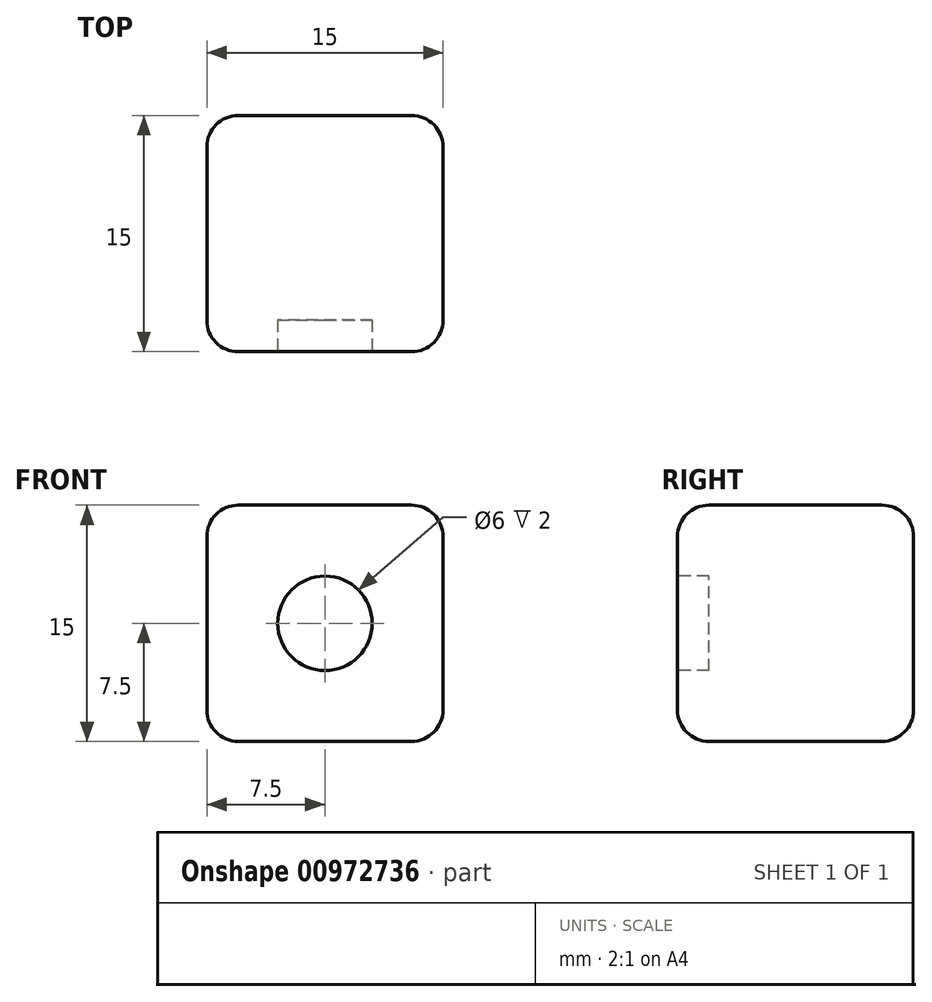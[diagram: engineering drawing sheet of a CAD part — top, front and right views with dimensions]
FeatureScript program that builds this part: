
annotation { "Feature Type Name" : "Feature", "Feature Type Description" : "" }
export const myFeature = defineFeature(function(context is Context, id is Id, definition is map)
    precondition{}
    {
        {
            var Q0;
            Q0=qCreatedBy(makeId("Front.planeOp"),FACE);
            var sketch = newSketch(context, id + "F0", { "sketchPlane" : qUnion([Q0])});
            skLineSegment(sketch, "E0.bottom", {"start": v(-7.5, 7.5) * mm, "end": v(7.5, 7.5) * mm});
            skLineSegment(sketch, "E0.top", {"start": v(-7.5, -7.5) * mm, "end": v(7.5, -7.5) * mm});
            skLineSegment(sketch, "E0.left", {"start": v(-7.5, 7.5) * mm, "end": v(-7.5, -7.5) * mm});
            skLineSegment(sketch, "E0.right", {"start": v(7.5, 7.5) * mm, "end": v(7.5, -7.5) * mm});
            skLineSegment(sketch, "E1", {"start": v(-7.5, 0) * mm, "end": v(7.5, 0) * mm, "construction": true});
            skLineSegment(sketch, "E2", {"start": v(0, 7.5) * mm, "end": v(0, -7.5) * mm, "construction": true});
            skPoint(sketch, "E3", {"position": v(0, 0) * mm});
            skSolve(sketch);
        }
        {
            var Q0;
            Q0=makeQuery(id+"F0.imprint","IMPRINT",FACE,{"disambiguationData":[TD([[makeQuery(id+"F0.imprint","IMPRINT",EDGE,{"derivedFrom":sQuery(id+"F0.wireOp",EDGE,"E0.bottom")}),-1.0]])]});
            extrude(context, id + "F1", {"entities" : qUnion([Q0]), "oppositeDirection" : true, "depth" : 15 * mm, "offsetDistance" : 25.4 * mm});
        }
        {
            var Q0;
            Q0=makeQuery(id+"F1.opExtrude","SWEPT_FACE",FACE,{"disambiguationData":[OSD([sQuery(id+"F0.wireOp",EDGE,"E0.bottom")])]});
            var Q1;
            Q1=makeQuery(id+"F1.opExtrude","SWEPT_FACE",FACE,{"disambiguationData":[OSD([sQuery(id+"F0.wireOp",EDGE,"E0.right")])]});
            var Q2;
            Q2=makeQuery(id+"F1.opExtrude","CAP_FACE",FACE,{"disambiguationData":[OSD([sQuery(id+"F0.wireOp",EDGE,"E0.bottom"),sQuery(id+"F0.wireOp",EDGE,"E0.top"),sQuery(id+"F0.wireOp",EDGE,"E0.left"),sQuery(id+"F0.wireOp",EDGE,"E0.right")])],"isStart":true});
            var Q3;
            Q3=makeQuery(id+"F1.opExtrude","SWEPT_FACE",FACE,{"disambiguationData":[OSD([sQuery(id+"F0.wireOp",EDGE,"E0.top")])]});
            var Q4;
            Q4=makeQuery(id+"F1.opExtrude","SWEPT_FACE",FACE,{"disambiguationData":[OSD([sQuery(id+"F0.wireOp",EDGE,"E0.left")])]});
            var Q5;
            Q5=makeQuery(id+"F1.opExtrude","CAP_FACE",FACE,{"disambiguationData":[OSD([sQuery(id+"F0.wireOp",EDGE,"E0.bottom"),sQuery(id+"F0.wireOp",EDGE,"E0.top"),sQuery(id+"F0.wireOp",EDGE,"E0.left"),sQuery(id+"F0.wireOp",EDGE,"E0.right")])],"isStart":false});
            fillet(context, id + "F2", {"entities" : qUnion([Q0, Q1, Q2, Q3, Q4, Q5]), "radius" : 2 * mm, "tangentPropagation" : true, "allowEdgeOverflow" : false});
        }
        {
            var Q0;
            Q0=makeQuery(id+"F1.opExtrude","CAP_FACE",FACE,{"disambiguationData":[OSD([sQuery(id+"F0.wireOp",EDGE,"E0.bottom"),sQuery(id+"F0.wireOp",EDGE,"E0.top"),sQuery(id+"F0.wireOp",EDGE,"E0.left"),sQuery(id+"F0.wireOp",EDGE,"E0.right")])],"isStart":true});
            var sketch = newSketch(context, id + "F3", { "sketchPlane" : qUnion([Q0])});
            skCircle(sketch, "E4", {"center": v(0, 0) * mm, "radius": 3 * mm});
            skSolve(sketch);
        }
        {
            var Q0;
            Q0=makeQuery(id+"F3.imprint","IMPRINT",FACE,{"disambiguationData":[TD([[makeQuery(id+"F3.imprint","IMPRINT",EDGE,{"derivedFrom":sQuery(id+"F3.wireOp",EDGE,"E4")}),1.0]])]});
            extrude(context, id + "F4", {"entities" : qUnion([Q0]), "operationType" : NewBodyOperationType.REMOVE, "oppositeDirection" : true, "depth" : 2 * mm, "offsetDistance" : 25.4 * mm});
        }
    });
